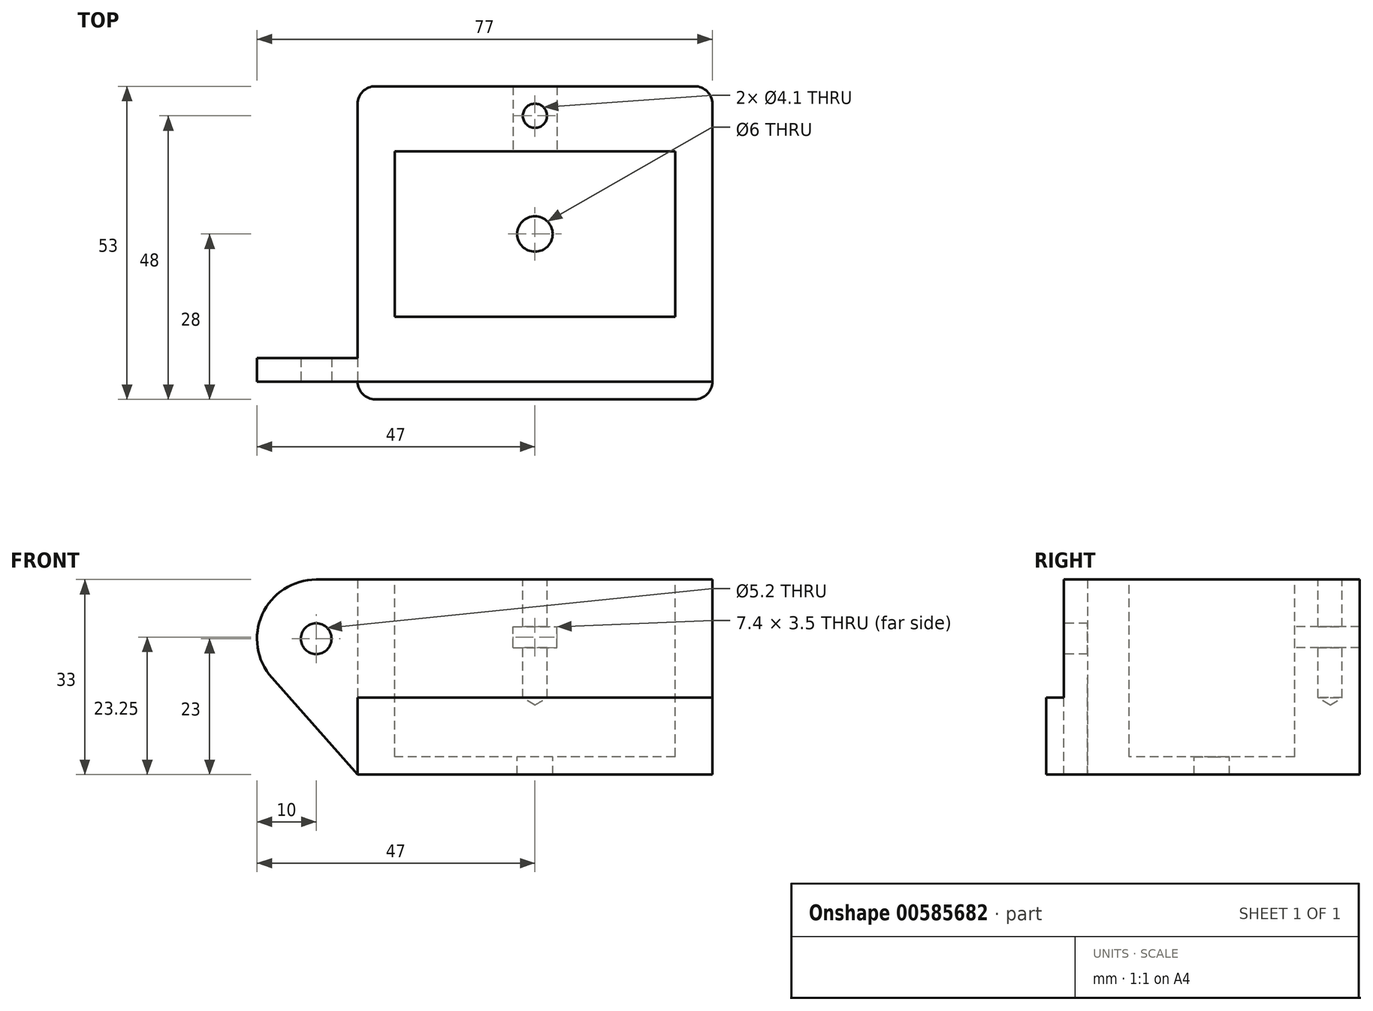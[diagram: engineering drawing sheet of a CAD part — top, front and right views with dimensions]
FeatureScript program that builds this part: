
annotation { "Feature Type Name" : "Feature", "Feature Type Description" : "" }
export const myFeature = defineFeature(function(context is Context, id is Id, definition is map)
    precondition{}
    {
        {
            var Q0;
            Q0=qCreatedBy(makeId("Top.planeOp"),FACE);
            var sketch = newSketch(context, id + "F0", { "sketchPlane" : qUnion([Q0])});
            skLineSegment(sketch, "E0.bottom", {"start": v(-30, 25) * mm, "end": v(30, 25) * mm});
            skLineSegment(sketch, "E0.top", {"start": v(-30, -25) * mm, "end": v(30, -25) * mm});
            skLineSegment(sketch, "E0.left", {"start": v(-30, 25) * mm, "end": v(-30, -25) * mm});
            skLineSegment(sketch, "E0.right", {"start": v(30, 25) * mm, "end": v(30, -25) * mm});
            skSolve(sketch);
        }
        {
            var Q0;
            Q0=makeQuery(id+"F0.imprint","IMPRINT",FACE,{"disambiguationData":[TD([[makeQuery(id+"F0.imprint","IMPRINT",EDGE,{"derivedFrom":sQuery(id+"F0.wireOp",EDGE,"E0.bottom")}),-1.0]])]});
            extrude(context, id + "F1", {"entities" : qUnion([Q0]), "depth" : 33 * mm, "offsetDistance" : 25 * mm});
        }
        {
            var Q0;
            Q0=makeQuery(id+"F1.opExtrude","CAP_FACE",FACE,{"disambiguationData":[OSD([sQuery(id+"F0.wireOp",EDGE,"E0.bottom"),sQuery(id+"F0.wireOp",EDGE,"E0.top"),sQuery(id+"F0.wireOp",EDGE,"E0.left"),sQuery(id+"F0.wireOp",EDGE,"E0.right")])],"isStart":false});
            var sketch = newSketch(context, id + "F2", { "sketchPlane" : qUnion([Q0])});
            skLineSegment(sketch, "E1.bottom", {"start": v(23.7, 14) * mm, "end": v(-23.7, 14) * mm});
            skLineSegment(sketch, "E1.top", {"start": v(23.7, -14) * mm, "end": v(-23.7, -14) * mm});
            skLineSegment(sketch, "E1.left", {"start": v(23.7, 14) * mm, "end": v(23.7, -14) * mm});
            skLineSegment(sketch, "E1.right", {"start": v(-23.7, 14) * mm, "end": v(-23.7, -14) * mm});
            skSolve(sketch);
        }
        {
            var Q0;
            Q0 = qSketchRegion(id + "F2", true);
            extrude(context, id + "F3", {"entities" : qUnion([Q0]), "operationType" : NewBodyOperationType.REMOVE, "oppositeDirection" : true, "depth" : 30 * mm, "offsetDistance" : 25 * mm});
        }
        {
            var Q0;
            Q0=makeQuery(id+"F1.opExtrude","CAP_FACE",FACE,{"disambiguationData":[OSD([sQuery(id+"F0.wireOp",EDGE,"E0.bottom"),sQuery(id+"F0.wireOp",EDGE,"E0.top"),sQuery(id+"F0.wireOp",EDGE,"E0.left"),sQuery(id+"F0.wireOp",EDGE,"E0.right")])],"isStart":false});
            var sketch = newSketch(context, id + "F4", { "sketchPlane" : qUnion([Q0])});
            skPoint(sketch, "E2", {"position": v(0, 20) * mm});
            skPoint(sketch, "E2.positionSnap0", {"position": v(0, 14) * mm});
            skSolve(sketch);
        }
        {
            var Q0;
            Q0=sQuery(id+"F4.wireOp",VERTEX,"E2");
            var Q1;
            Q1=makeQuery(id+"F1.opExtrude","SWEPT_BODY",BODY,{"disambiguationData":[OSD([sQuery(id+"F0.wireOp",EDGE,"E0.bottom"),sQuery(id+"F0.wireOp",EDGE,"E0.top"),sQuery(id+"F0.wireOp",EDGE,"E0.left"),sQuery(id+"F0.wireOp",EDGE,"E0.right")])]});
            hole(context, id + "F5", {"style" : HoleStyle.SIMPLE, "endStyle" : HoleEndStyle.BLIND, "holeDiameter" : 4.1 * mm, "majorDiameter" : 5 * mm, "holeDepth" : 20 * mm, "isTappedThrough" : true, "tappedDepth" : 12 * mm, "tapClearance" : 3, "startFromSketch" : true, "locations" : qUnion([Q0]), "scope" : qUnion([Q1])});
        }
        {
            var Q0;
            Q0=makeQuery(id+"F1.opExtrude","CAP_FACE",FACE,{"disambiguationData":[OSD([sQuery(id+"F0.wireOp",EDGE,"E0.bottom"),sQuery(id+"F0.wireOp",EDGE,"E0.top"),sQuery(id+"F0.wireOp",EDGE,"E0.left"),sQuery(id+"F0.wireOp",EDGE,"E0.right")])],"isStart":false});
            cPlane(context, id + "F6", {"entities" : qUnion([Q0]), "cplaneType" : CPlaneType.OFFSET, "offset" : 8 * mm, "oppositeDirection" : true, "width" : 150 * mm, "height" : 150 * mm});
        }
        {
            var Q0;
            Q0=qCreatedBy(id+"F6.planeOp",FACE);
            var sketch = newSketch(context, id + "F7", { "sketchPlane" : qUnion([Q0])});
            skPoint(sketch, "E3.0", {"position": v(0, 20) * mm});
            skLineSegment(sketch, "E4.bottom", {"start": v(-3.7, 25) * mm, "end": v(3.7, 25) * mm});
            skLineSegment(sketch, "E4.top", {"start": v(-3.7, 14) * mm, "end": v(3.7, 14) * mm});
            skLineSegment(sketch, "E4.left", {"start": v(-3.7, 25) * mm, "end": v(-3.7, 14) * mm});
            skLineSegment(sketch, "E4.right", {"start": v(3.7, 25) * mm, "end": v(3.7, 14) * mm});
            skSolve(sketch);
        }
        {
            var Q0;
            Q0 = qSketchRegion(id + "F7", true);
            extrude(context, id + "F8", {"entities" : qUnion([Q0]), "operationType" : NewBodyOperationType.REMOVE, "oppositeDirection" : true, "depth" : 3.5 * mm, "offsetDistance" : 25 * mm});
        }
        {
            var Q0;
            Q0=makeQuery(id+"F1.opExtrude","SWEPT_FACE",FACE,{"disambiguationData":[OSD([sQuery(id+"F0.wireOp",EDGE,"E0.top")])]});
            var sketch = newSketch(context, id + "F9", { "sketchPlane" : qUnion([Q0])});
            skArc(sketch, "E5", {"start": v(-37, 33) * mm, "mid": v(-46.12, 27.1) * mm, "end": v(-44.49, 16.37) * mm});
            skLineSegment(sketch, "E6", {"start": v(-30, 33) * mm, "end": v(-37, 33) * mm});
            skLineSegment(sketch, "E7", {"start": v(-30, 0) * mm, "end": v(-44.49, 16.37) * mm});
            skLineSegment(sketch, "E8", {"start": v(-30, 33) * mm, "end": v(-30, 0) * mm});
            skCircle(sketch, "E9", {"center": v(-37, 23) * mm, "radius": 2.6 * mm});
            skSolve(sketch);
        }
        {
            var Q0;
            Q0 = qSketchRegion(id + "F9", true);
            extrude(context, id + "F10", {"entities" : qUnion([Q0]), "operationType" : NewBodyOperationType.ADD, "oppositeDirection" : true, "depth" : 4 * mm, "offsetDistance" : 25 * mm});
        }
        {
            var Q0;
            Q0=makeQuery(id+"F3.boolean.opBoolean","COPY",FACE,{"derivedFrom":makeQuery(id+"F3.opExtrude","CAP_FACE",FACE,{"disambiguationData":[OSD([sQuery(id+"F2.wireOp",EDGE,"E1.bottom"),sQuery(id+"F2.wireOp",EDGE,"E1.top"),sQuery(id+"F2.wireOp",EDGE,"E1.left"),sQuery(id+"F2.wireOp",EDGE,"E1.right")])],"isStart":false})});
            var sketch = newSketch(context, id + "F11", { "sketchPlane" : qUnion([Q0])});
            skPoint(sketch, "E10", {"position": v(0, 0) * mm});
            skSolve(sketch);
        }
        {
            var Q0;
            Q0=sQuery(id+"F11.wireOp",VERTEX,"E10");
            var Q1;
            Q1=makeQuery(id+"F1.opExtrude","SWEPT_BODY",BODY,{"disambiguationData":[OSD([sQuery(id+"F0.wireOp",EDGE,"E0.bottom"),sQuery(id+"F0.wireOp",EDGE,"E0.top"),sQuery(id+"F0.wireOp",EDGE,"E0.left"),sQuery(id+"F0.wireOp",EDGE,"E0.right")])]});
            hole(context, id + "F12", {"style" : HoleStyle.SIMPLE, "endStyle" : HoleEndStyle.THROUGH, "holeDiameter" : 6 * mm, "majorDiameter" : 5 * mm, "isTappedThrough" : true, "tappedDepth" : 12 * mm, "tapClearance" : 3, "startFromSketch" : true, "locations" : qUnion([Q0]), "scope" : qUnion([Q1])});
        }
        {
            var Q0;
            {var subQ0=sQuery(id+"F9.wireOp",EDGE,"E9");var subQ1=sQuery(id+"F9.wireOp",EDGE,"E8");var subQ2=sQuery(id+"F9.wireOp",EDGE,"E7");var subQ3=sQuery(id+"F9.wireOp",EDGE,"E6");var subQ4=sQuery(id+"F9.wireOp",EDGE,"E5");Q0=makeQuery(id+"FxGcfdmfdCKY0Wt_1.1.F10.boolean.opBoolean","MERGE",FACE,{"derivedFrom":[makeQuery(id+"F10.boolean.opBoolean","MERGE",FACE,{"derivedFrom":[makeQuery(id+"F1.opExtrude","SWEPT_FACE",FACE,{"disambiguationData":[OSD([sQuery(id+"F0.wireOp",EDGE,"E0.top")])]}),makeQuery(id+"F10.opExtrude","CAP_FACE",FACE,{"disambiguationData":[OSD([subQ4,subQ3,subQ2,subQ1,subQ0])],"isStart":true})]}),makeQuery(id+"FxGcfdmfdCKY0Wt_1.1.F10.opExtrude","CAP_FACE",FACE,{"disambiguationData":[OSD([subQ4,subQ3,subQ2,subQ1,subQ0])],"isStart":true})]});}
            var sketch = newSketch(context, id + "F13", { "sketchPlane" : qUnion([Q0])});
            skLineSegment(sketch, "E11.bottom", {"start": v(-30, 0) * mm, "end": v(30, 0) * mm});
            skLineSegment(sketch, "E11.top", {"start": v(-30, 13) * mm, "end": v(30, 13) * mm});
            skLineSegment(sketch, "E11.left", {"start": v(-30, 0) * mm, "end": v(-30, 13) * mm});
            skLineSegment(sketch, "E11.right", {"start": v(30, 0) * mm, "end": v(30, 13) * mm});
            skSolve(sketch);
        }
        {
            var Q0;
            Q0=makeQuery(id+"F13.imprint","IMPRINT",FACE,{"disambiguationData":[TD([[makeQuery(id+"F13.imprint","IMPRINT",EDGE,{"derivedFrom":sQuery(id+"F13.wireOp",EDGE,"E11.bottom")}),1.0]])]});
            extrude(context, id + "F14", {"entities" : qUnion([Q0]), "operationType" : NewBodyOperationType.ADD, "depth" : 3 * mm, "offsetDistance" : 25 * mm});
        }
        {
            var Q0;
            Q0=makeQuery(id+"F14.opExtrude","CAP_EDGE",EDGE,{"disambiguationData":[OSD([sQuery(id+"F13.wireOp",EDGE,"E11.left")])],"isStart":false});
            var Q1;
            Q1=makeQuery(id+"F14.opExtrude","CAP_EDGE",EDGE,{"disambiguationData":[OSD([sQuery(id+"F13.wireOp",EDGE,"E11.right")])],"isStart":false});
            var Q2;
            Q2=makeQuery(id+"F1.opExtrude","SWEPT_EDGE",EDGE,{"disambiguationData":[OSD([sQuery(id+"F0.wireOp",EDGE,"E0.bottom"),sQuery(id+"F0.wireOp",EDGE,"E0.left")])]});
            var Q3;
            Q3=makeQuery(id+"F1.opExtrude","SWEPT_EDGE",EDGE,{"disambiguationData":[OSD([sQuery(id+"F0.wireOp",EDGE,"E0.bottom"),sQuery(id+"F0.wireOp",EDGE,"E0.right")])]});
            fillet(context, id + "F15", {"entities" : qUnion([Q0, Q1, Q2, Q3]), "radius" : 3 * mm, "tangentPropagation" : true, "allowEdgeOverflow" : false});
        }
    });
